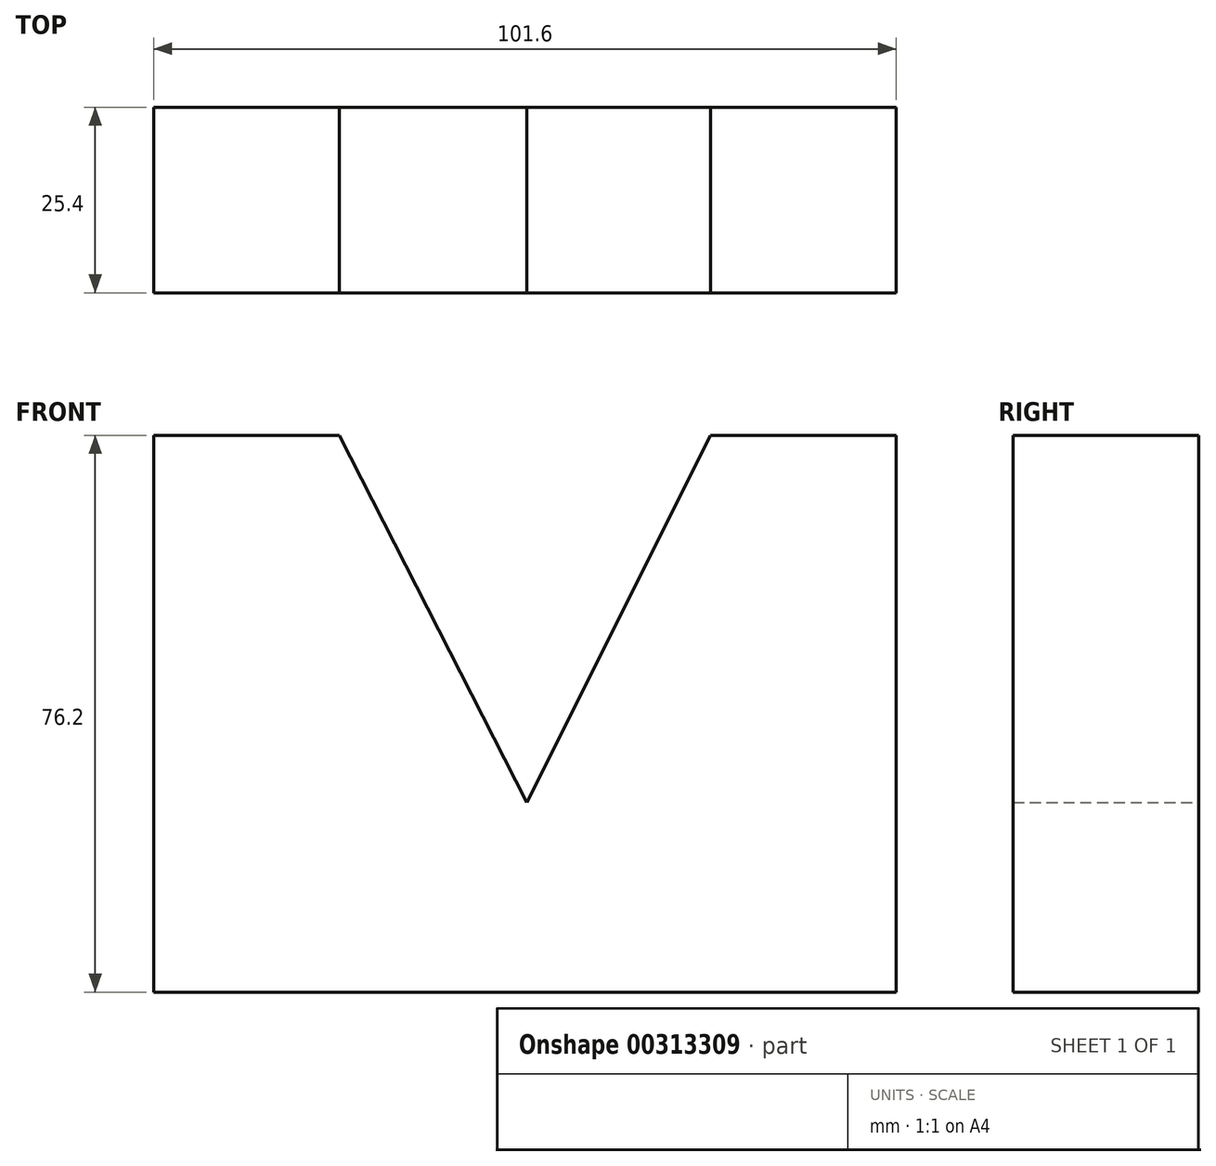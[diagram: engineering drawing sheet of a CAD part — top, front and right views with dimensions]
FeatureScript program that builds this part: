
annotation { "Feature Type Name" : "Feature", "Feature Type Description" : "" }
export const myFeature = defineFeature(function(context is Context, id is Id, definition is map)
    precondition{}
    {
        {
            var Q0;
            Q0=qCreatedBy(makeId("Front.planeOp"),FACE);
            var sketch = newSketch(context, id + "F0", { "sketchPlane" : qUnion([Q0])});
            skLineSegment(sketch, "E0", {"start": v(-51.07, -40.59) * mm, "end": v(50.53, -40.59) * mm});
            skLineSegment(sketch, "E1", {"start": v(50.53, -40.59) * mm, "end": v(50.53, 35.61) * mm});
            skLineSegment(sketch, "E2", {"start": v(50.53, 35.61) * mm, "end": v(25.13, 35.61) * mm});
            skLineSegment(sketch, "E3", {"start": v(25.13, 35.61) * mm, "end": v(0, -14.64) * mm});
            skLineSegment(sketch, "E4", {"start": v(0, -14.64) * mm, "end": v(-25.67, 35.61) * mm});
            skLineSegment(sketch, "E5", {"start": v(-25.67, 35.61) * mm, "end": v(-51.07, 35.61) * mm});
            skLineSegment(sketch, "E6", {"start": v(-51.07, 35.61) * mm, "end": v(-51.07, -40.59) * mm});
            skSolve(sketch);
        }
        {
            var Q0;
            Q0=makeQuery(id+"F0.imprint","IMPRINT",FACE,{"disambiguationData":[TD([[makeQuery(id+"F0.imprint","IMPRINT",EDGE,{"derivedFrom":sQuery(id+"F0.wireOp",EDGE,"E0")}),1.0]])]});
            extrude(context, id + "F1", {"entities" : qUnion([Q0]), "depth" : 25.4 * mm});
        }
    });
